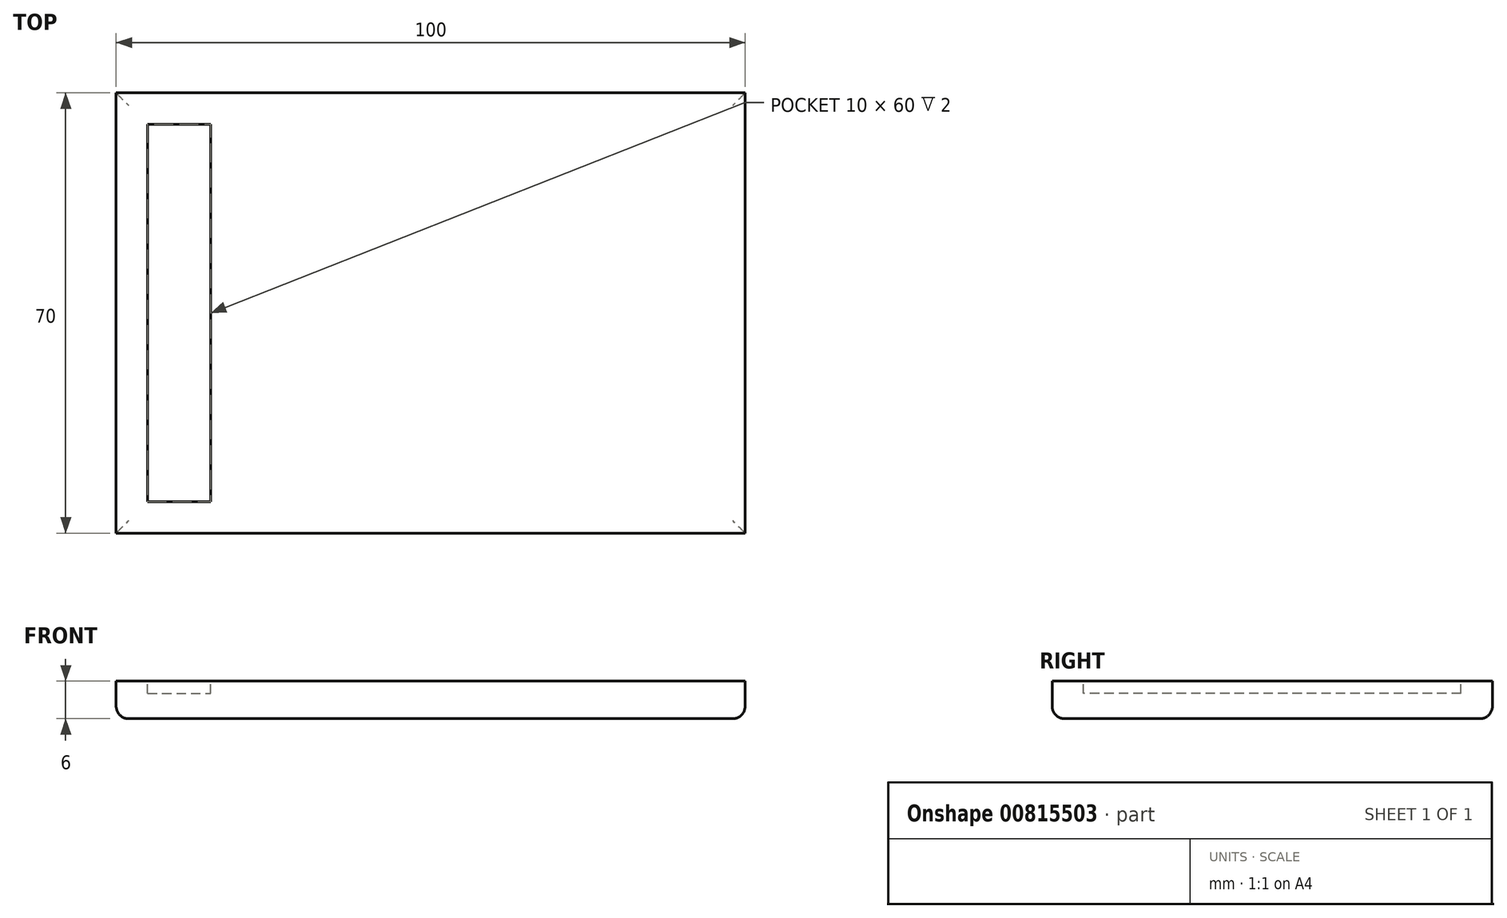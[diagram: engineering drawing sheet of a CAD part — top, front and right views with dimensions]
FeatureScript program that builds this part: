
annotation { "Feature Type Name" : "Feature", "Feature Type Description" : "" }
export const myFeature = defineFeature(function(context is Context, id is Id, definition is map)
    precondition{}
    {
        {
            var Q0;
            Q0=qCreatedBy(makeId("Top.planeOp"),FACE);
            var sketch = newSketch(context, id + "F0", { "sketchPlane" : qUnion([Q0])});
            skLineSegment(sketch, "E0.bottom", {"start": v(50, 35) * mm, "end": v(-50, 35) * mm});
            skLineSegment(sketch, "E0.top", {"start": v(50, -35) * mm, "end": v(-50, -35) * mm});
            skLineSegment(sketch, "E0.left", {"start": v(50, 35) * mm, "end": v(50, -35) * mm});
            skLineSegment(sketch, "E0.right", {"start": v(-50, 35) * mm, "end": v(-50, -35) * mm});
            skPoint(sketch, "E0.middle", {"position": v(0, 0) * mm});
            skSolve(sketch);
        }
        {
            var Q0;
            Q0=makeQuery(id+"F0.imprint","IMPRINT",FACE,{"disambiguationData":[TD([[makeQuery(id+"F0.imprint","IMPRINT",EDGE,{"derivedFrom":sQuery(id+"F0.wireOp",EDGE,"E0.bottom")}),1.0]])]});
            extrude(context, id + "F1", {"entities" : qUnion([Q0]), "depth" : 6 * mm, "offsetDistance" : 25 * mm});
        }
        {
            var Q0;
            Q0=makeQuery(id+"F1.opExtrude","CAP_EDGE",EDGE,{"disambiguationData":[OSD([sQuery(id+"F0.wireOp",EDGE,"E0.top")])],"isStart":true});
            var Q1;
            Q1=makeQuery(id+"F1.opExtrude","CAP_EDGE",EDGE,{"disambiguationData":[OSD([sQuery(id+"F0.wireOp",EDGE,"E0.left")])],"isStart":true});
            var Q2;
            Q2=makeQuery(id+"F1.opExtrude","CAP_EDGE",EDGE,{"disambiguationData":[OSD([sQuery(id+"F0.wireOp",EDGE,"E0.bottom")])],"isStart":true});
            var Q3;
            Q3=makeQuery(id+"F1.opExtrude","CAP_EDGE",EDGE,{"disambiguationData":[OSD([sQuery(id+"F0.wireOp",EDGE,"E0.right")])],"isStart":true});
            fillet(context, id + "F2", {"entities" : qUnion([Q0, Q1, Q2, Q3]), "radius" : 2 * mm, "tangentPropagation" : true, "allowEdgeOverflow" : false});
        }
        {
            var Q0;
            Q0=makeQuery(id+"F1.opExtrude","CAP_FACE",FACE,{"disambiguationData":[OSD([sQuery(id+"F0.wireOp",EDGE,"E0.bottom"),sQuery(id+"F0.wireOp",EDGE,"E0.top"),sQuery(id+"F0.wireOp",EDGE,"E0.left"),sQuery(id+"F0.wireOp",EDGE,"E0.right")])],"isStart":false});
            var sketch = newSketch(context, id + "F3", { "sketchPlane" : qUnion([Q0])});
            skLineSegment(sketch, "E1.bottom", {"start": v(-45, 30) * mm, "end": v(-35, 30) * mm});
            skLineSegment(sketch, "E1.top", {"start": v(-45, -30) * mm, "end": v(-35, -30) * mm});
            skLineSegment(sketch, "E1.left", {"start": v(-45, 30) * mm, "end": v(-45, -30) * mm});
            skLineSegment(sketch, "E1.right", {"start": v(-35, 30) * mm, "end": v(-35, -30) * mm});
            skPoint(sketch, "E1.middle", {"position": v(-40, 0) * mm});
            skSolve(sketch);
        }
        {
            var Q0;
            Q0=makeQuery(id+"F3.imprint","IMPRINT",FACE,{"disambiguationData":[TD([[makeQuery(id+"F3.imprint","IMPRINT",EDGE,{"derivedFrom":sQuery(id+"F3.wireOp",EDGE,"E1.bottom")}),-1.0]])]});
            extrude(context, id + "F4", {"entities" : qUnion([Q0]), "operationType" : NewBodyOperationType.REMOVE, "oppositeDirection" : true, "depth" : 2 * mm, "offsetDistance" : 25 * mm});
        }
    });
